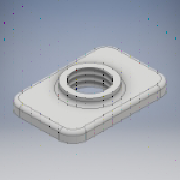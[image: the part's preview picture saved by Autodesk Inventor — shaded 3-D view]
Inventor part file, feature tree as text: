
AUTODESK INVENTOR PART (.ipt)
format: ipt  version: 2018 (Build 220112000, 112)  size: 175,616 bytes
history: native  units: mm
features: extrude x2, fillet x2, sketch x2, thread x1
ambient origin geometry x8: Origin, YZ Plane, XZ Plane, XY Plane, X Axis, Y Axis, Z Axis, Center Point
bodies: Solid1 (feature_tree)
feature tree (7):
  extrude  "Extrusion1"  Depth=15.0mm
  extrude  "Extrusion2"  Depth=2.0mm
  fillet  "Fillet1"  Radius=1.5mm
  thread  "Thread1"  [1 undecoded]
  fillet  "Fillet2"  Radius=1.0mm
  sketch  "Sketch1"  dims[d0=10.0mm d1=15.0mm]
  sketch  "Sketch2"  dims[d2=4.8mm d3=2.0mm d4=1.5mm d5=0.0mm d6=6.5mm d7=1.0mm d8=0.0mm d9=0.5mm d10=10.0mm d11=0.0mm d12=0.5mm]
note: 1 required parameter value undecoded (feature->parameter linkage not recoverable at this tier; creation-order binding heuristic only, values carry confidence <= 0.55)
